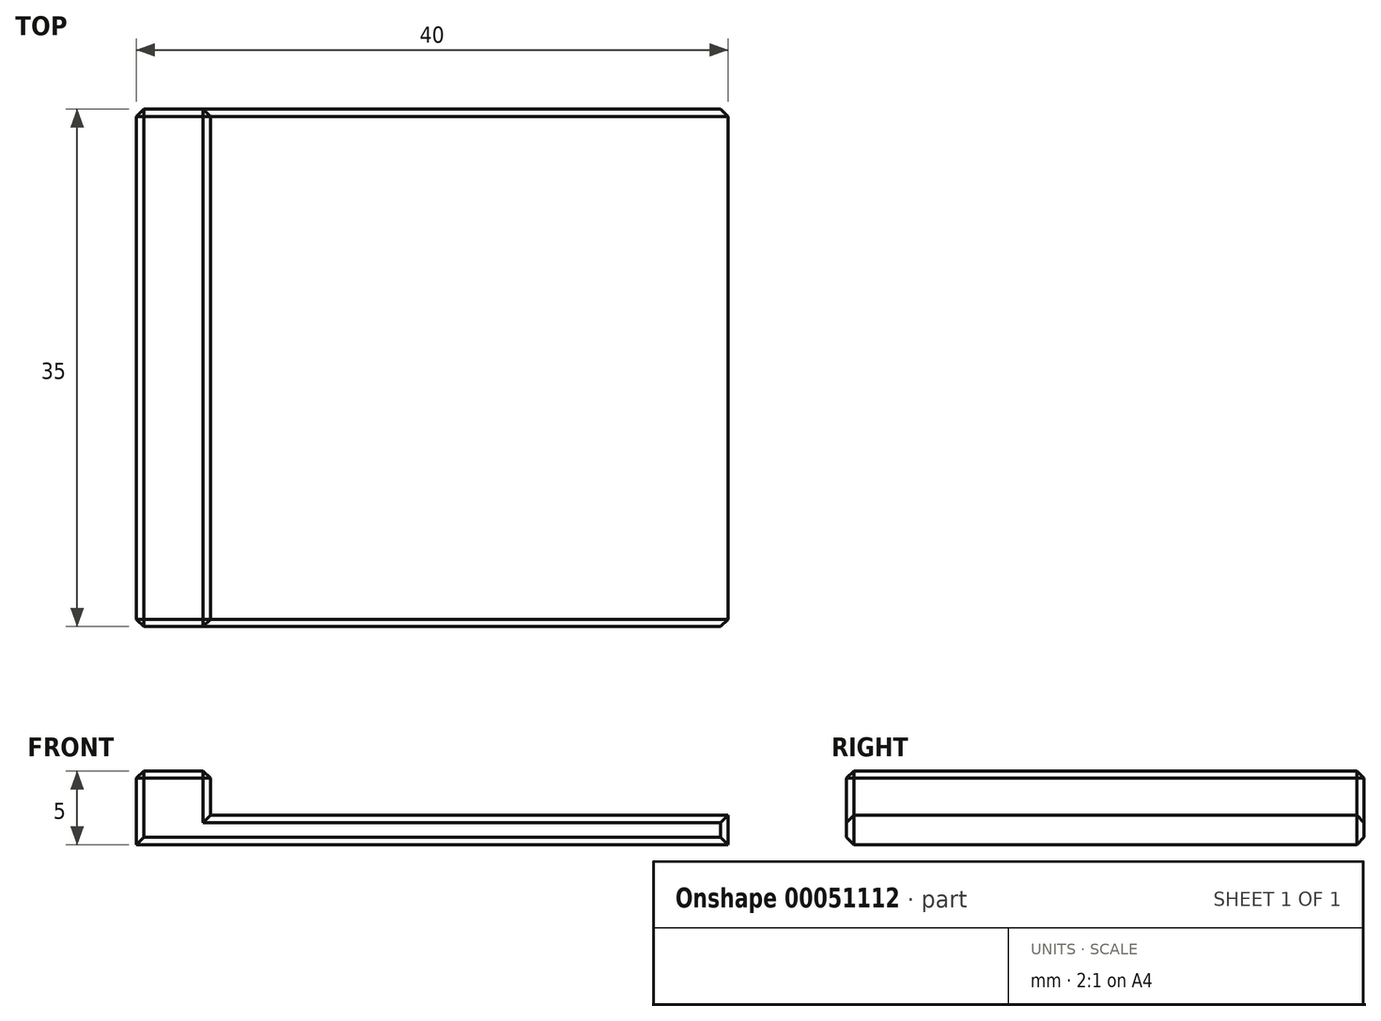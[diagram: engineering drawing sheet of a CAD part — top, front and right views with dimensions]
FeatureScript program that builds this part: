
annotation { "Feature Type Name" : "Feature", "Feature Type Description" : "" }
export const myFeature = defineFeature(function(context is Context, id is Id, definition is map)
    precondition{}
    {
        {
            var Q0;
            Q0=qCreatedBy(makeId("Top.planeOp"),FACE);
            var sketch = newSketch(context, id + "F0", { "sketchPlane" : qUnion([Q0])});
            skLineSegment(sketch, "E0.bottom", {"start": v(0, 0) * mm, "end": v(40, 0) * mm});
            skLineSegment(sketch, "E0.top", {"start": v(0, 35) * mm, "end": v(40, 35) * mm});
            skLineSegment(sketch, "E0.left", {"start": v(0, 0) * mm, "end": v(0, 35) * mm});
            skLineSegment(sketch, "E0.right", {"start": v(40, 0) * mm, "end": v(40, 35) * mm});
            skSolve(sketch);
        }
        {
            var Q0;
            Q0 = qSketchRegion(id + "F0", true);
            extrude(context, id + "F1", {"entities" : qUnion([Q0]), "depth" : 5 * mm});
        }
        {
            var Q0;
            Q0=makeQuery(id+"F1.opExtrude","CAP_FACE",FACE,{"disambiguationData":[OSD([sQuery(id+"F0.wireOp",EDGE,"E0.bottom"),sQuery(id+"F0.wireOp",EDGE,"E0.top"),sQuery(id+"F0.wireOp",EDGE,"E0.left"),sQuery(id+"F0.wireOp",EDGE,"E0.right")])],"isStart":false});
            var sketch = newSketch(context, id + "F2", { "sketchPlane" : qUnion([Q0])});
            skLineSegment(sketch, "E1.bottom", {"start": v(5, 35) * mm, "end": v(40, 35) * mm});
            skLineSegment(sketch, "E1.top", {"start": v(5, 0) * mm, "end": v(40, 0) * mm});
            skLineSegment(sketch, "E1.left", {"start": v(5, 35) * mm, "end": v(5, 0) * mm});
            skLineSegment(sketch, "E1.right", {"start": v(40, 35) * mm, "end": v(40, 0) * mm});
            skSolve(sketch);
        }
        {
            var Q0;
            Q0 = qSketchRegion(id + "F2", true);
            extrude(context, id + "F3", {"entities" : qUnion([Q0]), "operationType" : NewBodyOperationType.REMOVE, "oppositeDirection" : true, "depth" : 3 * mm});
        }
        {
            var Q0;
            Q0=makeQuery(id+"F1.opExtrude","CAP_FACE",FACE,{"disambiguationData":[OSD([sQuery(id+"F0.wireOp",EDGE,"E0.bottom"),sQuery(id+"F0.wireOp",EDGE,"E0.top"),sQuery(id+"F0.wireOp",EDGE,"E0.left"),sQuery(id+"F0.wireOp",EDGE,"E0.right")])],"isStart":false});
            var Q1;
            Q1=makeQuery(id+"F1.opExtrude","SWEPT_FACE",FACE,{"disambiguationData":[OSD([sQuery(id+"F0.wireOp",EDGE,"E0.bottom")])]});
            var Q2;
            Q2=makeQuery(id+"F1.opExtrude","SWEPT_FACE",FACE,{"disambiguationData":[OSD([sQuery(id+"F0.wireOp",EDGE,"E0.top")])]});
            chamfer(context, id + "F4", {"entities" : qUnion([Q0, Q1, Q2]), "width" : 0.5 * mm, "tangentPropagation" : true});
        }
    });
